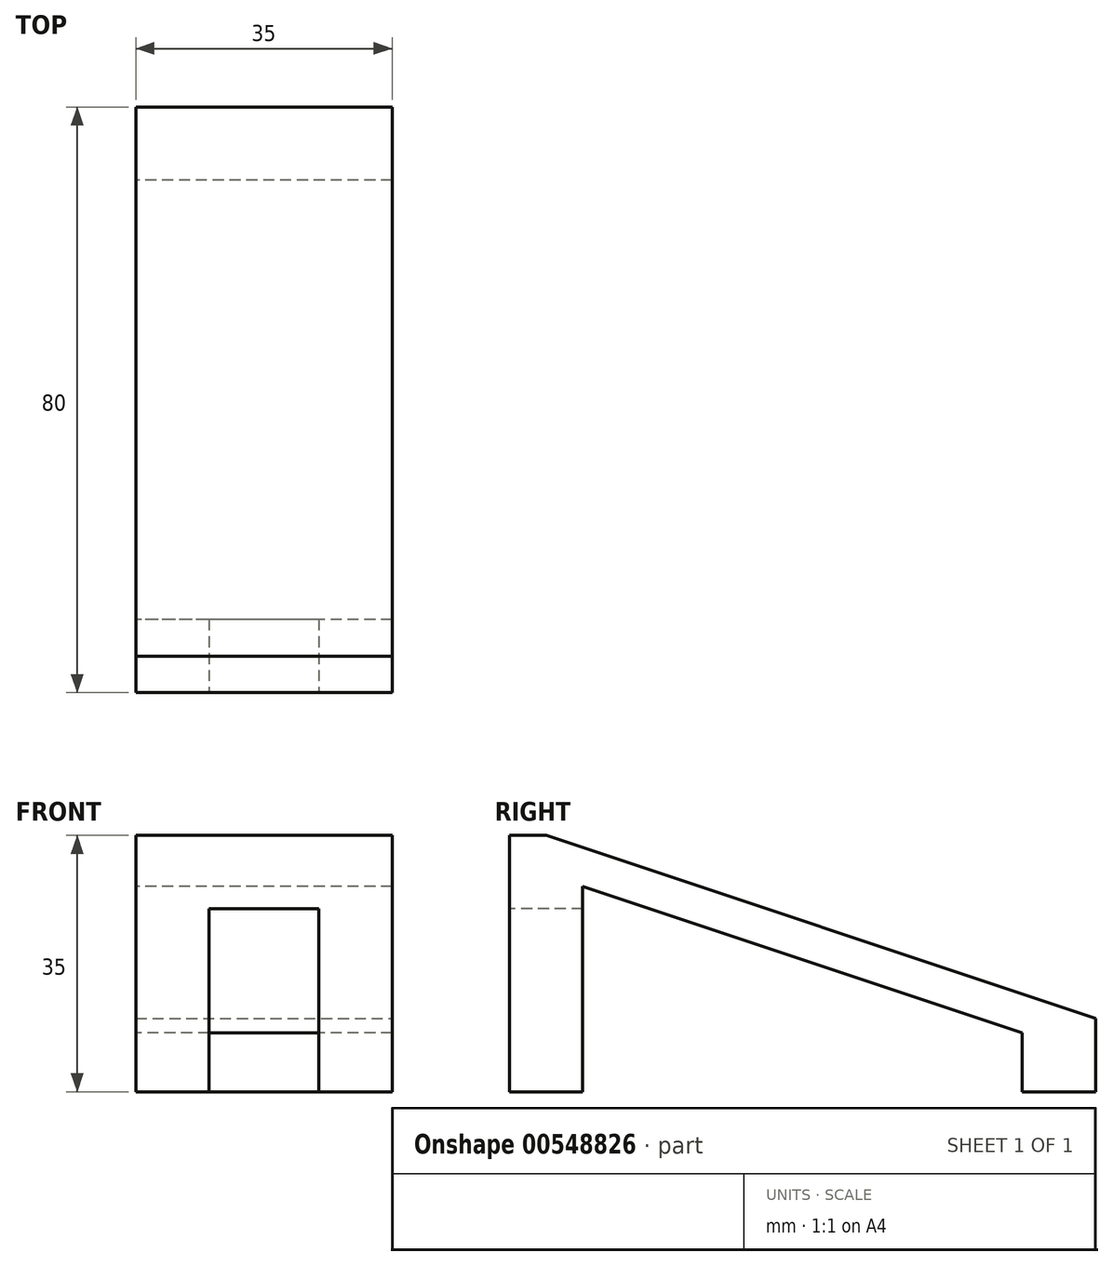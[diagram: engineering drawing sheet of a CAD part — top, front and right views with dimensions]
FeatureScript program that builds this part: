
annotation { "Feature Type Name" : "Feature", "Feature Type Description" : "" }
export const myFeature = defineFeature(function(context is Context, id is Id, definition is map)
    precondition{}
    {
        {
            var Q0;
            Q0=qCreatedBy(makeId("Top.planeOp"),FACE);
            var sketch = newSketch(context, id + "F0", { "sketchPlane" : qUnion([Q0])});
            skLineSegment(sketch, "E0.bottom", {"start": v(17.5, 17.5) * mm, "end": v(-17.5, 17.5) * mm});
            skLineSegment(sketch, "E0.top", {"start": v(17.5, -62.5) * mm, "end": v(-17.5, -62.5) * mm});
            skLineSegment(sketch, "E0.left", {"start": v(17.5, 17.5) * mm, "end": v(17.5, -62.5) * mm});
            skLineSegment(sketch, "E0.right", {"start": v(-17.5, 17.5) * mm, "end": v(-17.5, -62.5) * mm});
            skPoint(sketch, "E0.middle", {"position": v(0, -22.5) * mm});
            skSolve(sketch);
        }
        {
            var Q0;
            Q0=makeQuery(id+"F0.imprint","IMPRINT",FACE,{"disambiguationData":[TD([[makeQuery(id+"F0.imprint","IMPRINT",EDGE,{"derivedFrom":sQuery(id+"F0.wireOp",EDGE,"E0.bottom")}),1.0]])]});
            extrude(context, id + "F1", {"entities" : qUnion([Q0]), "depth" : 35 * mm, "offsetDistance" : 25 * mm});
        }
        {
            var Q0;
            Q0=makeQuery(id+"F1.opExtrude","CAP_EDGE",EDGE,{"disambiguationData":[OSD([sQuery(id+"F0.wireOp",EDGE,"E0.bottom")])],"isStart":false});
            chamfer(context, id + "F2", {"entities" : qUnion([Q0]), "chamferType" : ChamferType.TWO_OFFSETS, "width1" : 75 * mm, "oppositeDirection" : false, "width2" : 25 * mm, "tangentPropagation" : true});
        }
        {
            var Q0;
            Q0=makeQuery(id+"F1.opExtrude","SWEPT_FACE",FACE,{"disambiguationData":[OSD([sQuery(id+"F0.wireOp",EDGE,"E0.right")])]});
            var sketch = newSketch(context, id + "F3", { "sketchPlane" : qUnion([Q0])});
            skLineSegment(sketch, "E1", {"start": v(-7.5, 0) * mm, "end": v(-7.5, 8.06) * mm});
            skLineSegment(sketch, "E2", {"start": v(-7.5, 8.06) * mm, "end": v(52.5, 28.06) * mm});
            skLineSegment(sketch, "E3", {"start": v(52.5, 0) * mm, "end": v(52.5, 28.06) * mm});
            skSolve(sketch);
        }
        {
            var Q0;
            {var subQ0=sQuery(id+"F3.wireOp",EDGE,"E1");Q0=makeQuery(id+"F3.imprint","IMPRINT",FACE,{"disambiguationData":[TD([[makeQuery(id+"F3.imprint","IMPRINT",EDGE,{"derivedFrom":subQ0}),-1.0]])]});}
            extrude(context, id + "F4", {"entities" : qUnion([Q0]), "operationType" : NewBodyOperationType.REMOVE, "endBound" : BoundingType.THROUGH_ALL, "oppositeDirection" : true, "depth" : 25 * mm, "offsetDistance" : 25 * mm});
        }
        {
            var Q0;
            Q0=makeQuery(id+"F1.opExtrude","SWEPT_FACE",FACE,{"disambiguationData":[OSD([sQuery(id+"F0.wireOp",EDGE,"E0.top")])]});
            var sketch = newSketch(context, id + "F5", { "sketchPlane" : qUnion([Q0])});
            skLineSegment(sketch, "E4.bottom", {"start": v(7.5, 0) * mm, "end": v(-7.5, 0) * mm});
            skLineSegment(sketch, "E4.top", {"start": v(7.5, 25) * mm, "end": v(-7.5, 25) * mm});
            skLineSegment(sketch, "E4.left", {"start": v(7.5, 0) * mm, "end": v(7.5, 25) * mm});
            skLineSegment(sketch, "E4.right", {"start": v(-7.5, 0) * mm, "end": v(-7.5, 25) * mm});
            skSolve(sketch);
        }
        {
            var Q0;
            Q0=makeQuery(id+"F5.imprint","IMPRINT",FACE,{"disambiguationData":[TD([[makeQuery(id+"F5.imprint","IMPRINT",EDGE,{"derivedFrom":sQuery(id+"F5.wireOp",EDGE,"E4.bottom")}),-1.0]])]});
            extrude(context, id + "F6", {"entities" : qUnion([Q0]), "operationType" : NewBodyOperationType.REMOVE, "oppositeDirection" : true, "depth" : 10 * mm, "offsetDistance" : 25 * mm});
        }
    });
